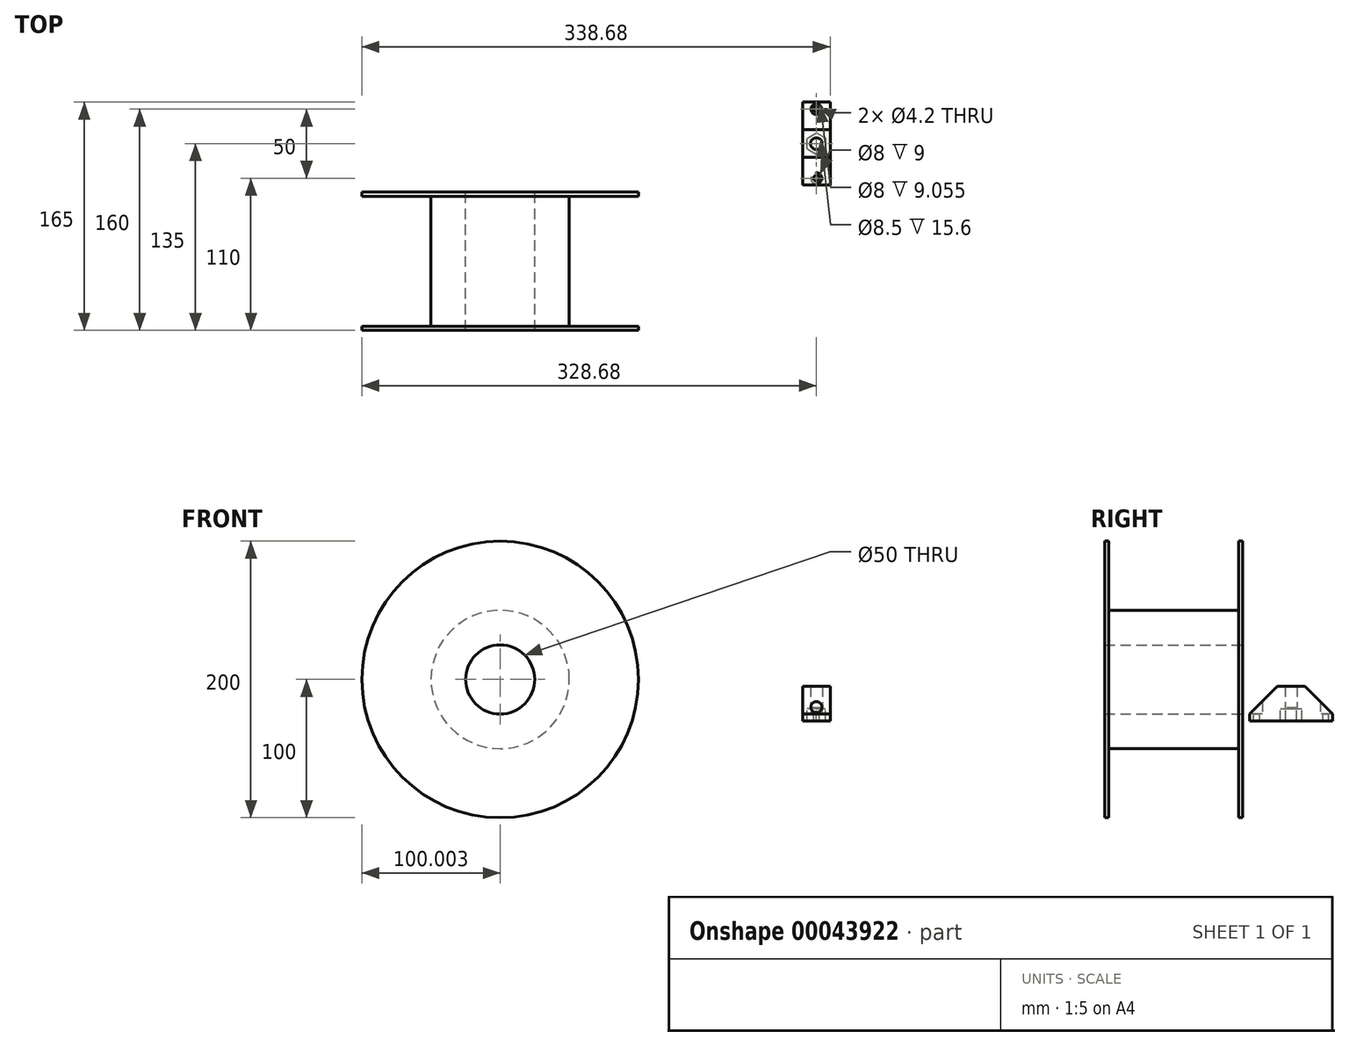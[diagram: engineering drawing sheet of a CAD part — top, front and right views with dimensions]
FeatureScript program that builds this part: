
annotation { "Feature Type Name" : "Feature", "Feature Type Description" : "" }
export const myFeature = defineFeature(function(context is Context, id is Id, definition is map)
    precondition{}
    {
        {
            var Q0;
            Q0=qCreatedBy(makeId("Front.planeOp"),FACE);
            var sketch = newSketch(context, id + "F0", { "sketchPlane" : qUnion([Q0])});
            skLineSegment(sketch, "E0.rect.bottom", {"start": v(-10, 30) * mm, "end": v(10, 30) * mm});
            skLineSegment(sketch, "E0.rect.top", {"start": v(-10, -30) * mm, "end": v(10, -30) * mm});
            skLineSegment(sketch, "E0.rect.left", {"start": v(-10, 30) * mm, "end": v(-10, -30) * mm});
            skLineSegment(sketch, "E0.rect.right", {"start": v(10, 30) * mm, "end": v(10, -30) * mm});
            skPoint(sketch, "E0.rect.middle", {"position": v(0, 0) * mm});
            skCircle(sketch, "E1.cCircle", {"center": v(0, 0) * mm, "radius": 6.75 * mm, "construction": true});
            skLineSegment(sketch, "E1.0", {"start": v(-6.75, -3.9) * mm, "end": v(-6.75, 3.9) * mm});
            skLineSegment(sketch, "E1.1", {"start": v(-6.75, 3.9) * mm, "end": v(0, 7.8) * mm});
            skLineSegment(sketch, "E1.2", {"start": v(0, 7.8) * mm, "end": v(6.75, 3.9) * mm});
            skLineSegment(sketch, "E1.3", {"start": v(6.75, 3.9) * mm, "end": v(6.75, -3.9) * mm});
            skLineSegment(sketch, "E1.4", {"start": v(6.75, -3.9) * mm, "end": v(0, -7.8) * mm});
            skLineSegment(sketch, "E1.5", {"start": v(0, -7.8) * mm, "end": v(-6.75, -3.9) * mm});
            skPoint(sketch, "E1.0.midPoint", {"position": v(-6.75, 0) * mm});
            skCircle(sketch, "E2", {"center": v(0, 25) * mm, "radius": 2.1 * mm});
            skCircle(sketch, "E3", {"center": v(0, -25) * mm, "radius": 2.1 * mm});
            skSolve(sketch);
        }
        {
            var Q0;
            Q0=makeQuery(id+"F0.imprint","IMPRINT",FACE,{"disambiguationData":[TD([[makeQuery(id+"F0.imprint","IMPRINT",EDGE,{"derivedFrom":sQuery(id+"F0.wireOp",EDGE,"E0.rect.bottom")}),-1.0]])]});
            var Q1;
            Q1=makeQuery(id+"F0.imprint","IMPRINT",FACE,{"disambiguationData":[TD([[makeQuery(id+"F0.imprint","IMPRINT",EDGE,{"derivedFrom":sQuery(id+"F0.wireOp",EDGE,"E2")}),1.0]])]});
            var Q2;
            Q2=makeQuery(id+"F0.imprint","IMPRINT",FACE,{"disambiguationData":[TD([[makeQuery(id+"F0.imprint","IMPRINT",EDGE,{"derivedFrom":sQuery(id+"F0.wireOp",EDGE,"E1.0")}),-1.0]])]});
            var Q3;
            Q3=makeQuery(id+"F0.imprint","IMPRINT",FACE,{"disambiguationData":[TD([[makeQuery(id+"F0.imprint","IMPRINT",EDGE,{"derivedFrom":sQuery(id+"F0.wireOp",EDGE,"E3")}),1.0]])]});
            extrude(context, id + "F1", {"entities" : qUnion([Q0, Q1, Q2, Q3]), "depth" : 20 * mm});
        }
        {
            var Q0;
            Q0=makeQuery(id+"F1.opExtrude","CAP_EDGE",EDGE,{"disambiguationData":[OSD([sQuery(id+"F0.wireOp",EDGE,"E0.rect.top")])],"isStart":false});
            var Q1;
            Q1=makeQuery(id+"F1.opExtrude","CAP_EDGE",EDGE,{"disambiguationData":[OSD([sQuery(id+"F0.wireOp",EDGE,"E0.rect.bottom")])],"isStart":false});
            chamfer(context, id + "F2", {"entities" : qUnion([Q0, Q1]), "chamferType" : ChamferType.TWO_OFFSETS, "width1" : 20 * mm, "oppositeDirection" : false, "width2" : 20 * mm, "tangentPropagation" : true});
        }
        {
            var Q0;
            Q0=qSketchRegion(id+"F0",true);
            extrude(context, id + "F3", {"entities" : qUnion([Q0]), "operationType" : NewBodyOperationType.ADD, "oppositeDirection" : true, "depth" : 5 * mm});
        }
        {
            var Q0;
            Q0=makeQuery(id+"F3.boolean.opBoolean","SPLIT",FACE,{"disambiguationData":[TD([makeQuery(id+"F3.opExtrude","SWEPT_FACE",FACE,{"disambiguationData":[OSD([sQuery(id+"F0.wireOp",EDGE,"E1.0")])]})])],"derivedFrom":makeQuery(id+"F1.opExtrude","CAP_FACE",FACE,{"disambiguationData":[OSD([sQuery(id+"F0.wireOp",EDGE,"E0.rect.bottom"),sQuery(id+"F0.wireOp",EDGE,"E0.rect.top"),sQuery(id+"F0.wireOp",EDGE,"E0.rect.left"),sQuery(id+"F0.wireOp",EDGE,"E0.rect.right")])],"isStart":true})});
            extrude(context, id + "F4", {"entities" : qUnion([Q0]), "operationType" : NewBodyOperationType.REMOVE, "oppositeDirection" : true, "depth" : 4 * mm});
        }
        {
            var Q0;
            Q0=makeQuery(id+"F3.boolean.opBoolean","SPLIT",FACE,{"disambiguationData":[TD([makeQuery(id+"F3.opExtrude","SWEPT_FACE",FACE,{"disambiguationData":[OSD([sQuery(id+"F0.wireOp",EDGE,"E3")])]})])],"derivedFrom":makeQuery(id+"F1.opExtrude","CAP_FACE",FACE,{"disambiguationData":[OSD([sQuery(id+"F0.wireOp",EDGE,"E0.rect.bottom"),sQuery(id+"F0.wireOp",EDGE,"E0.rect.top"),sQuery(id+"F0.wireOp",EDGE,"E0.rect.left"),sQuery(id+"F0.wireOp",EDGE,"E0.rect.right")])],"isStart":true})});
            var sketch = newSketch(context, id + "F5", { "sketchPlane" : qUnion([Q0])});
            skCircle(sketch, "E4", {"center": v(0, -25) * mm, "radius": 4 * mm});
            skCircle(sketch, "E5", {"center": v(0, 25) * mm, "radius": 4 * mm});
            skSolve(sketch);
        }
        {
            var Q0;
            Q0=qSketchRegion(id+"F5",true);
            extrude(context, id + "F6", {"entities" : qUnion([Q0]), "operationType" : NewBodyOperationType.REMOVE, "oppositeDirection" : true, "depth" : 25 * mm});
        }
        {
            var Q0;
            Q0=makeQuery(id+"F4.boolean.opBoolean","COPY",FACE,{"derivedFrom":makeQuery(id+"F4.opExtrude","CAP_FACE",FACE,{"disambiguationData":[OSD([sQuery(id+"F0.wireOp",EDGE,"E0.rect.bottom"),sQuery(id+"F0.wireOp",EDGE,"E0.rect.top"),sQuery(id+"F0.wireOp",EDGE,"E0.rect.left"),sQuery(id+"F0.wireOp",EDGE,"E0.rect.right")])],"isStart":false})});
            var sketch = newSketch(context, id + "F7", { "sketchPlane" : qUnion([Q0])});
            skCircle(sketch, "E6", {"center": v(0, 0) * mm, "radius": 4.25 * mm});
            skSolve(sketch);
        }
        {
            var Q0;
            Q0=qSketchRegion(id+"F7",true);
            var Q1;
            Q1=makeQuery(id+"F1.opExtrude","CAP_FACE",FACE,{"disambiguationData":[OSD([sQuery(id+"F0.wireOp",EDGE,"E0.rect.bottom"),sQuery(id+"F0.wireOp",EDGE,"E0.rect.top"),sQuery(id+"F0.wireOp",EDGE,"E0.rect.left"),sQuery(id+"F0.wireOp",EDGE,"E0.rect.right")])],"isStart":false});
            extrude(context, id + "F8", {"entities" : qUnion([Q0]), "operationType" : NewBodyOperationType.REMOVE, "endBound" : BoundingType.UP_TO_SURFACE, "oppositeDirection" : true, "endBoundEntityFace" : qUnion([Q1]), "depth" : 25 * mm, "hasSecondDirection" : true, "secondDirectionOppositeDirection" : true, "secondDirectionDepth" : 0.4 * mm});
        }
        {
            var Q0;
            Q0=qCreatedBy(makeId("Front.planeOp"),FACE);
            var sketch = newSketch(context, id + "F9", { "sketchPlane" : qUnion([Q0])});
            skCircle(sketch, "E7", {"center": v(-228.68, 0) * mm, "radius": 100 * mm});
            skCircle(sketch, "E8", {"center": v(-228.68, 0) * mm, "radius": 25 * mm});
            skCircle(sketch, "E9", {"center": v(-228.68, 0) * mm, "radius": 50 * mm});
            skSolve(sketch);
        }
        {
            var Q0;
            Q0=makeQuery(id+"F9.imprint","IMPRINT",FACE,{"disambiguationData":[TD([[makeQuery(id+"F9.imprint","IMPRINT",EDGE,{"derivedFrom":sQuery(id+"F9.wireOp",EDGE,"E7")}),1.0]])]});
            extrude(context, id + "F10", {"entities" : qUnion([Q0]), "depth" : 3 * mm});
        }
        {
            var Q0;
            Q0=makeQuery(id+"F9.imprint","IMPRINT",FACE,{"disambiguationData":[TD([[makeQuery(id+"F9.imprint","IMPRINT",EDGE,{"derivedFrom":sQuery(id+"F9.wireOp",EDGE,"E8")}),-1.0]])]});
            extrude(context, id + "F11", {"entities" : qUnion([Q0]), "operationType" : NewBodyOperationType.ADD, "depth" : 100 * mm});
        }
        {
            var Q0;
            Q0=makeQuery(id+"F10.opExtrude","CAP_FACE",FACE,{"disambiguationData":[OSD([sQuery(id+"F9.wireOp",EDGE,"E7"),sQuery(id+"F9.wireOp",EDGE,"E9")])],"isStart":false});
            extrude(context, id + "F12", {"entities" : qUnion([Q0]), "operationType" : NewBodyOperationType.ADD, "depth" : 97 * mm, "hasSecondDirection" : true, "secondDirectionOppositeDirection" : false, "secondDirectionDepth" : 94 * mm});
        }
        {
            var Q0;
            Q0=makeQuery(id+"F1.opExtrude","SWEPT_BODY",BODY,{"disambiguationData":[OSD([sQuery(id+"F0.wireOp",EDGE,"E0.rect.bottom"),sQuery(id+"F0.wireOp",EDGE,"E0.rect.top"),sQuery(id+"F0.wireOp",EDGE,"E0.rect.left"),sQuery(id+"F0.wireOp",EDGE,"E0.rect.right")])]});
            var Q1;
            Q1=makeQuery(id+"F3.opExtrude","CAP_EDGE",EDGE,{"disambiguationData":[OSD([sQuery(id+"F0.wireOp",EDGE,"E0.rect.top")])],"isStart":false});
            transform(context, id + "F13", {"entities" : qUnion([Q0]), "transformType" : TransformType.ROTATION, "transformAxis" : qUnion([Q1]), "angle" : 90 * degree, "oppositeDirection" : true, "makeCopy" : false});
        }
    });
